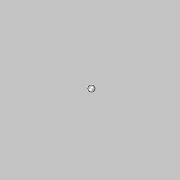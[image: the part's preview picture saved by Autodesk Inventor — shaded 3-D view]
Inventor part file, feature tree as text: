
AUTODESK INVENTOR PART (.ipt)
format: ipt  version: 2017 (Build 210142000, 142)  size: 111,104 bytes
history: native  units: mm
features: extrude x6, sketch x6, projected_geometry x1
ambient origin geometry x8: Origin, YZ Plane, XZ Plane, XY Plane, X Axis, Y Axis, Z Axis, Center Point
bodies: Solid1 (feature_tree)
feature tree (13):
  extrude  "Extrusion1"  Depth=180.0mm
  extrude  "Extrusion2"  Depth=5.0mm TaperAngle=0.0deg
  extrude  "Extrusion3"  Depth=64.0mm
  extrude  "Extrusion4"  Depth=5.0mm TaperAngle=0.0deg
  extrude  "Extrusion5"  Depth=4.0mm
  extrude  "Extrusion6"  Depth=15.0mm
  sketch  "Sketch1"  dims[d0=125.0mm d1=180.0mm]
  sketch  "Sketch2"  dims[d2=60.0mm d3=-0.349066mm d4=5.0mm d5=0.0mm]
  sketch  "Sketch3"  dims[d6=40.0mm d7=0.0mm d8=64.0mm]
  projected_geometry  "Projected Loop1"
  sketch  "Sketch4"  dims[d9=64.0mm d10=5.0mm d11=0.0mm]
  sketch  "Sketch5"  dims[d12=60.0mm d13=4.0mm]
  sketch  "Sketch6"  dims[d14=15.0mm d15=0.0mm d16=15.0mm d17=15.0mm d18=20.0mm d19=0.0mm d20=0.0mm]
